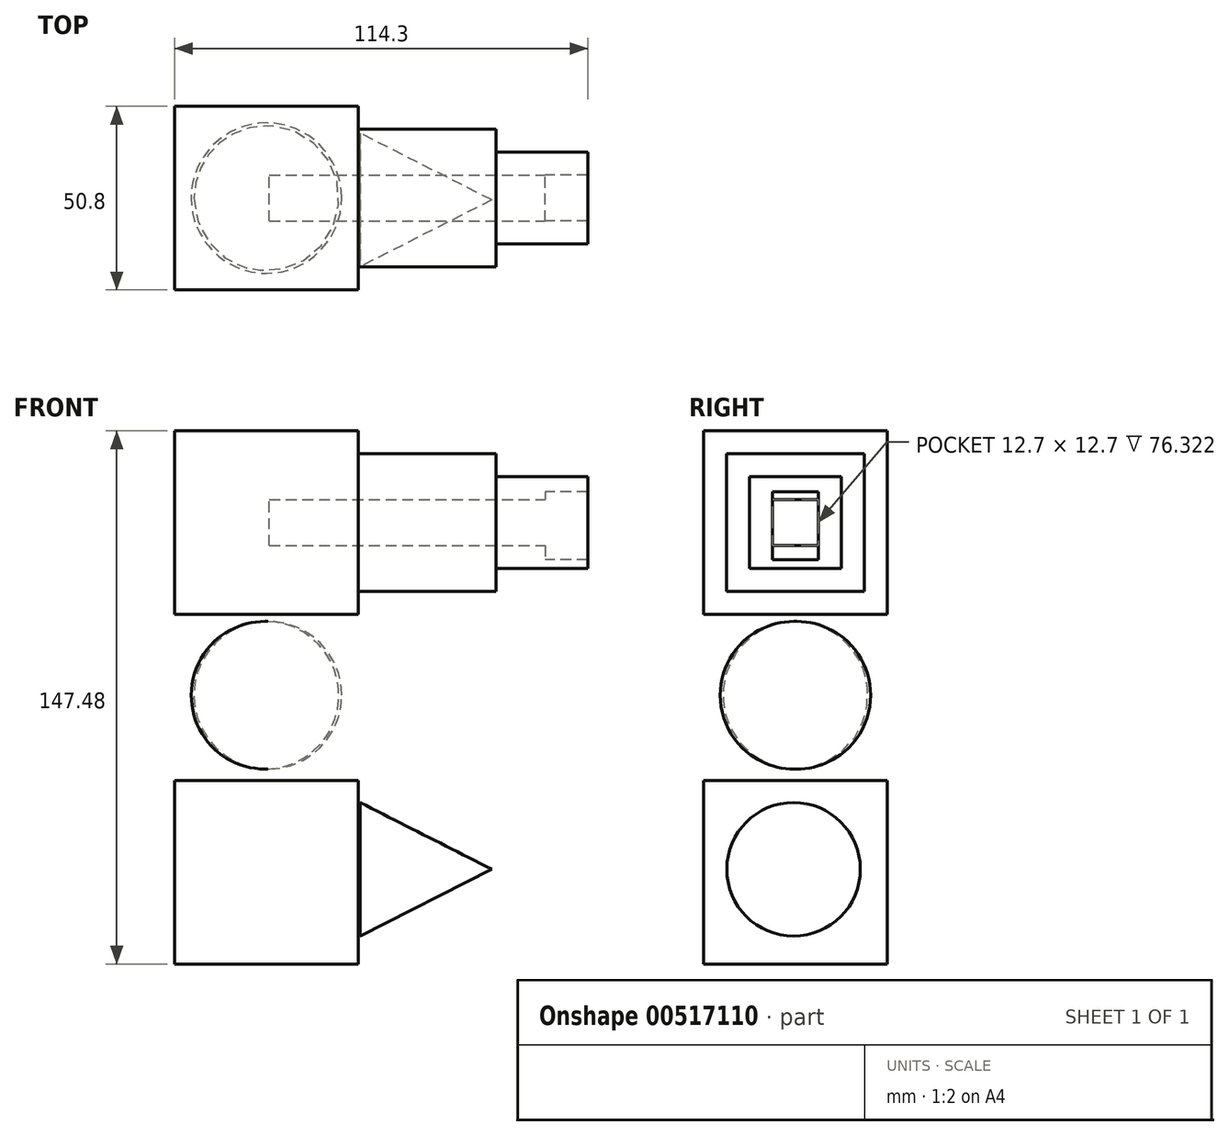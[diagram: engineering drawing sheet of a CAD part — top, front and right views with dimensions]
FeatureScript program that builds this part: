
annotation { "Feature Type Name" : "Feature", "Feature Type Description" : "" }
export const myFeature = defineFeature(function(context is Context, id is Id, definition is map)
    precondition{}
    {
        {
            var Q0;
            Q0=qCreatedBy(makeId("Front.planeOp"),FACE);
            var sketch = newSketch(context, id + "F0", { "sketchPlane" : qUnion([Q0])});
            skLineSegment(sketch, "E0.bottom", {"start": v(-25.4, 76.2) * mm, "end": v(25.4, 76.2) * mm});
            skLineSegment(sketch, "E0.top", {"start": v(-25.4, 25.4) * mm, "end": v(25.4, 25.4) * mm});
            skLineSegment(sketch, "E0.left", {"start": v(-25.4, 76.2) * mm, "end": v(-25.4, 25.4) * mm});
            skLineSegment(sketch, "E0.right", {"start": v(25.4, 76.2) * mm, "end": v(25.4, 25.4) * mm});
            skSolve(sketch);
        }
        {
            var Q0;
            Q0=makeQuery(id+"F0.imprint","IMPRINT",FACE,{"disambiguationData":[TD([[makeQuery(id+"F0.imprint","IMPRINT",EDGE,{"derivedFrom":sQuery(id+"F0.wireOp",EDGE,"E0.bottom")}),-1.0]])]});
            extrude(context, id + "F1", {"entities" : qUnion([Q0]), "depth" : 25.4 * mm, "offsetDistance" : 25.4 * mm});
        }
        {
            var Q0;
            Q0=qCreatedBy(makeId("Front.planeOp"),FACE);
            var sketch = newSketch(context, id + "F2", { "sketchPlane" : qUnion([Q0])});
            skLineSegment(sketch, "E1.bottom", {"start": v(-25.4, -20.48) * mm, "end": v(25.4, -20.48) * mm});
            skLineSegment(sketch, "E1.top", {"start": v(-25.4, -71.28) * mm, "end": v(25.4, -71.28) * mm});
            skLineSegment(sketch, "E1.left", {"start": v(-25.4, -20.48) * mm, "end": v(-25.4, -71.28) * mm});
            skLineSegment(sketch, "E1.right", {"start": v(25.4, -20.48) * mm, "end": v(25.4, -71.28) * mm});
            skSolve(sketch);
        }
        {
            var Q0;
            Q0=makeQuery(id+"F2.imprint","IMPRINT",FACE,{"disambiguationData":[TD([[makeQuery(id+"F2.imprint","IMPRINT",EDGE,{"derivedFrom":sQuery(id+"F2.wireOp",EDGE,"E1.bottom")}),-1.0]])]});
            extrude(context, id + "F3", {"entities" : qUnion([Q0]), "depth" : 25.4 * mm, "offsetDistance" : 25.4 * mm});
        }
        {
            var Q0;
            Q0=qCreatedBy(makeId("Front.planeOp"),FACE);
            var sketch = newSketch(context, id + "F4", { "sketchPlane" : qUnion([Q0])});
            skLineSegment(sketch, "E2", {"start": v(0, 23.5) * mm, "end": v(0, -17.34) * mm});
            skArc(sketch, "E3", {"start": v(0, -17.34) * mm, "mid": v(20.8, 3.08) * mm, "end": v(0, 23.5) * mm});
            skSolve(sketch);
        }
        {
            var Q0;
            Q0=makeQuery(id+"F4.imprint","IMPRINT",FACE,{"disambiguationData":[TD([[makeQuery(id+"F4.imprint","IMPRINT",EDGE,{"derivedFrom":sQuery(id+"F4.wireOp",EDGE,"E2")}),1.0]])]});
            var Q1;
            Q1=sQuery(id+"F4.wireOp",EDGE,"E2");
            revolve(context, id + "F5", {"entities" : qUnion([Q0]), "axis" : qUnion([Q1]), "revolveType" : RevolveType.FULL});
        }
        {
            var Q0;
            Q0=makeQuery(id+"F1.opExtrude","CAP_FACE",FACE,{"disambiguationData":[OSD([sQuery(id+"F0.wireOp",EDGE,"E0.bottom"),sQuery(id+"F0.wireOp",EDGE,"E0.top"),sQuery(id+"F0.wireOp",EDGE,"E0.left"),sQuery(id+"F0.wireOp",EDGE,"E0.right")])],"isStart":true});
            extrude(context, id + "F6", {"entities" : qUnion([Q0]), "operationType" : NewBodyOperationType.ADD, "depth" : 25.4 * mm, "offsetDistance" : 25.4 * mm});
        }
        {
            var Q0;
            Q0=makeQuery(id+"F2.imprint","IMPRINT",FACE,{"disambiguationData":[TD([[makeQuery(id+"F2.imprint","IMPRINT",EDGE,{"derivedFrom":sQuery(id+"F2.wireOp",EDGE,"E1.bottom")}),-1.0]])]});
            extrude(context, id + "F7", {"entities" : qUnion([Q0]), "operationType" : NewBodyOperationType.ADD, "depth" : 25.4 * mm, "offsetDistance" : 25.4 * mm});
        }
        {
            var Q0;
            Q0=makeQuery(id+"F3.opExtrude","CAP_FACE",FACE,{"disambiguationData":[OSD([sQuery(id+"F2.wireOp",EDGE,"E1.bottom"),sQuery(id+"F2.wireOp",EDGE,"E1.top"),sQuery(id+"F2.wireOp",EDGE,"E1.left"),sQuery(id+"F2.wireOp",EDGE,"E1.right")])],"isStart":true});
            extrude(context, id + "F8", {"entities" : qUnion([Q0]), "operationType" : NewBodyOperationType.ADD, "depth" : 25.4 * mm, "offsetDistance" : 25.4 * mm});
        }
        {
            var Q0;
            Q0=qCreatedBy(makeId("Front.planeOp"),FACE);
            var sketch = newSketch(context, id + "F9", { "sketchPlane" : qUnion([Q0])});
            skLineSegment(sketch, "E4.bottom", {"start": v(58.03, 59.3) * mm, "end": v(77.08, 59.3) * mm});
            skLineSegment(sketch, "E4.top", {"start": v(58.03, 40.58) * mm, "end": v(77.08, 40.58) * mm});
            skLineSegment(sketch, "E4.left", {"start": v(58.03, 59.3) * mm, "end": v(58.03, 40.58) * mm});
            skLineSegment(sketch, "E4.right", {"start": v(77.08, 59.3) * mm, "end": v(77.08, 40.58) * mm});
            skSolve(sketch);
        }
        {
            var Q0;
            Q0=makeQuery(id+"F9.imprint","IMPRINT",FACE,{"disambiguationData":[TD([[makeQuery(id+"F9.imprint","IMPRINT",EDGE,{"derivedFrom":sQuery(id+"F9.wireOp",EDGE,"E4.bottom")}),-1.0]])]});
            extrude(context, id + "F10", {"entities" : qUnion([Q0]), "operationType" : NewBodyOperationType.ADD, "depth" : 6.35 * mm, "offsetDistance" : 25.4 * mm});
        }
        {
            var Q0;
            Q0=makeQuery(id+"F10.opExtrude","CAP_FACE",FACE,{"disambiguationData":[OSD([sQuery(id+"F9.wireOp",EDGE,"E4.bottom"),sQuery(id+"F9.wireOp",EDGE,"E4.top"),sQuery(id+"F9.wireOp",EDGE,"E4.left"),sQuery(id+"F9.wireOp",EDGE,"E4.right")])],"isStart":true});
            extrude(context, id + "F11", {"entities" : qUnion([Q0]), "operationType" : NewBodyOperationType.ADD, "depth" : 6.35 * mm, "offsetDistance" : 25.4 * mm});
        }
        {
            var Q0;
            {var subQ0=sQuery(id+"F0.wireOp",EDGE,"E0.right");Q0=makeQuery(id+"F6.boolean.opBoolean","MERGE",FACE,{"derivedFrom":[makeQuery(id+"F1.opExtrude","SWEPT_FACE",FACE,{"disambiguationData":[OSD([subQ0])]}),makeQuery(id+"F6.opExtrude","SWEPT_FACE",FACE,{"disambiguationData":[OSD([subQ0])]})]});}
            var sketch = newSketch(context, id + "F12", { "sketchPlane" : qUnion([Q0])});
            skLineSegment(sketch, "E5.bottom", {"start": v(-19.05, 69.85) * mm, "end": v(19.05, 69.85) * mm});
            skLineSegment(sketch, "E5.top", {"start": v(-19.05, 31.75) * mm, "end": v(19.05, 31.75) * mm});
            skLineSegment(sketch, "E5.left", {"start": v(-19.05, 69.85) * mm, "end": v(-19.05, 31.75) * mm});
            skLineSegment(sketch, "E5.right", {"start": v(19.05, 69.85) * mm, "end": v(19.05, 31.75) * mm});
            skSolve(sketch);
        }
        {
            var Q0;
            Q0=makeQuery(id+"F12.imprint","IMPRINT",FACE,{"disambiguationData":[TD([[makeQuery(id+"F12.imprint","IMPRINT",EDGE,{"derivedFrom":sQuery(id+"F12.wireOp",EDGE,"E5.bottom")}),-1.0]])]});
            extrude(context, id + "F13", {"entities" : qUnion([Q0]), "operationType" : NewBodyOperationType.ADD, "depth" : 38.1 * mm, "offsetDistance" : 25.4 * mm});
        }
        {
            var Q0;
            Q0=makeQuery(id+"F13.opExtrude","CAP_FACE",FACE,{"disambiguationData":[OSD([sQuery(id+"F12.wireOp",EDGE,"E5.bottom"),sQuery(id+"F12.wireOp",EDGE,"E5.top"),sQuery(id+"F12.wireOp",EDGE,"E5.left"),sQuery(id+"F12.wireOp",EDGE,"E5.right")])],"isStart":false});
            var sketch = newSketch(context, id + "F14", { "sketchPlane" : qUnion([Q0])});
            skLineSegment(sketch, "E6.bottom", {"start": v(-12.7, 63.5) * mm, "end": v(12.7, 63.5) * mm});
            skLineSegment(sketch, "E6.top", {"start": v(-12.7, 38.1) * mm, "end": v(12.7, 38.1) * mm});
            skLineSegment(sketch, "E6.left", {"start": v(-12.7, 63.5) * mm, "end": v(-12.7, 38.1) * mm});
            skLineSegment(sketch, "E6.right", {"start": v(12.7, 63.5) * mm, "end": v(12.7, 38.1) * mm});
            skSolve(sketch);
        }
        {
            var Q0;
            Q0=makeQuery(id+"F14.imprint","IMPRINT",FACE,{"disambiguationData":[TD([[makeQuery(id+"F14.imprint","IMPRINT",EDGE,{"derivedFrom":sQuery(id+"F14.wireOp",EDGE,"E6.bottom")}),-1.0]])]});
            extrude(context, id + "F15", {"entities" : qUnion([Q0]), "operationType" : NewBodyOperationType.ADD, "depth" : 25.4 * mm, "offsetDistance" : 25.4 * mm});
        }
        {
            var Q0;
            Q0=makeQuery(id+"F15.opExtrude","CAP_FACE",FACE,{"disambiguationData":[OSD([sQuery(id+"F14.wireOp",EDGE,"E6.bottom"),sQuery(id+"F14.wireOp",EDGE,"E6.top"),sQuery(id+"F14.wireOp",EDGE,"E6.left"),sQuery(id+"F14.wireOp",EDGE,"E6.right")])],"isStart":false});
            var sketch = newSketch(context, id + "F16", { "sketchPlane" : qUnion([Q0])});
            skLineSegment(sketch, "E7.bottom", {"start": v(-6.35, 57.15) * mm, "end": v(6.35, 57.15) * mm});
            skLineSegment(sketch, "E7.top", {"start": v(-6.35, 44.45) * mm, "end": v(6.35, 44.45) * mm});
            skLineSegment(sketch, "E7.left", {"start": v(-6.35, 57.15) * mm, "end": v(-6.35, 44.45) * mm});
            skLineSegment(sketch, "E7.right", {"start": v(6.35, 57.15) * mm, "end": v(6.35, 44.45) * mm});
            skSolve(sketch);
        }
        {
            var Q0;
            Q0=makeQuery(id+"F16.imprint","IMPRINT",FACE,{"disambiguationData":[TD([[makeQuery(id+"F16.imprint","IMPRINT",EDGE,{"derivedFrom":sQuery(id+"F16.wireOp",EDGE,"E7.bottom")}),-1.0]])]});
            extrude(context, id + "F17", {"entities" : qUnion([Q0]), "operationType" : NewBodyOperationType.REMOVE, "oppositeDirection" : true, "depth" : 88.14 * mm, "offsetDistance" : 25.4 * mm});
        }
        {
            var Q0;
            Q0=qCreatedBy(makeId("Front.planeOp"),FACE);
            var sketch = newSketch(context, id + "F18", { "sketchPlane" : qUnion([Q0])});
            skLineSegment(sketch, "E8", {"start": v(25.93, -42.8) * mm, "end": v(62.3, -42.8) * mm});
            skLineSegment(sketch, "E9", {"start": v(62.3, -42.8) * mm, "end": v(25.93, -24.34) * mm});
            skLineSegment(sketch, "E10", {"start": v(25.93, -24.34) * mm, "end": v(25.93, -42.8) * mm});
            skSolve(sketch);
        }
        {
            var Q0;
            Q0=makeQuery(id+"F18.imprint","IMPRINT",FACE,{"disambiguationData":[TD([[makeQuery(id+"F18.imprint","IMPRINT",EDGE,{"derivedFrom":sQuery(id+"F18.wireOp",EDGE,"E8")}),1.0]])]});
            var Q1;
            Q1=sQuery(id+"F18.wireOp",EDGE,"E8");
            revolve(context, id + "F19", {"entities" : qUnion([Q0]), "axis" : qUnion([Q1]), "revolveType" : RevolveType.FULL});
        }
        {
            var Q0;
            Q0=makeQuery(id+"F19.opRevolve","SWEPT_BODY",BODY,{"disambiguationData":[OSD([sQuery(id+"F18.wireOp",EDGE,"E8"),sQuery(id+"F18.wireOp",EDGE,"E9"),sQuery(id+"F18.wireOp",EDGE,"E10")])]});
            transform(context, id + "F20", {"entities" : qUnion([Q0]), "transformType" : TransformType.TRANSLATION_3D, "dx" : 0 * mm, "dy" : -0.5 * mm, "dz" : -2.3 * mm, "makeCopy" : false});
        }
    });
